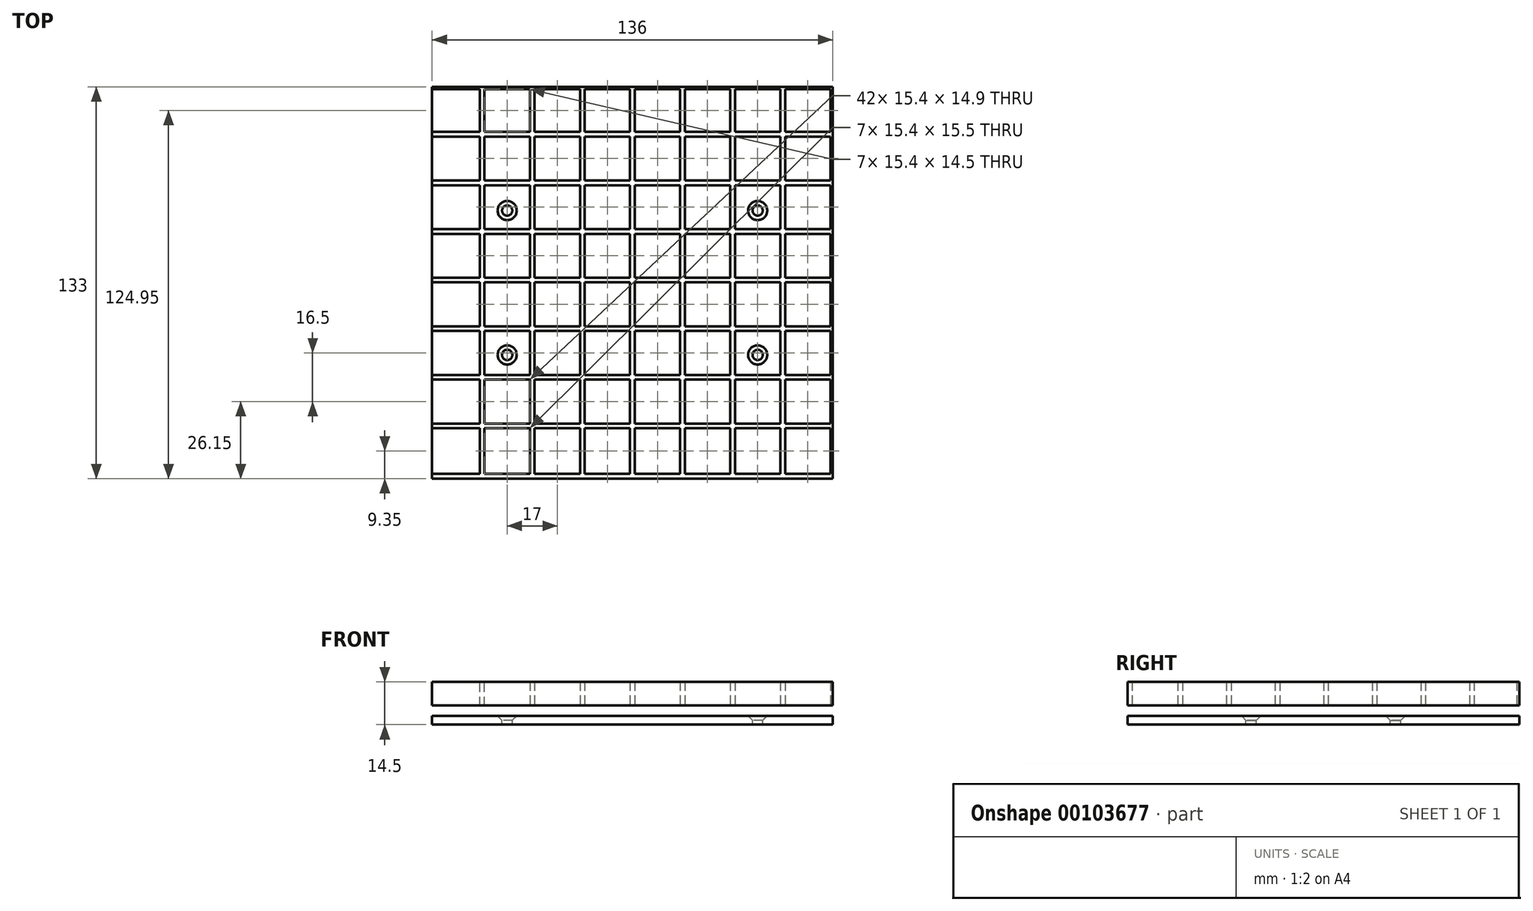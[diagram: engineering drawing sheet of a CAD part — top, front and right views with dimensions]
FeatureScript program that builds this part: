
annotation { "Feature Type Name" : "Feature", "Feature Type Description" : "" }
export const myFeature = defineFeature(function(context is Context, id is Id, definition is map)
    precondition{}
    {
        {
            var Q0;
            Q0=qCreatedBy(makeId("Front.planeOp"),FACE);
            var sketch = newSketch(context, id + "F0", { "sketchPlane" : qUnion([Q0])});
            skLineSegment(sketch, "E0.bottom", {"start": v(-68, 3) * mm, "end": v(68, 3) * mm});
            skLineSegment(sketch, "E0.top", {"start": v(-68, 0) * mm, "end": v(68, 0) * mm});
            skLineSegment(sketch, "E0.left", {"start": v(-68, 3) * mm, "end": v(-68, 0) * mm});
            skLineSegment(sketch, "E0.right", {"start": v(68, 3) * mm, "end": v(68, 0) * mm});
            skLineSegment(sketch, "E1.bottom", {"start": v(-68, 3) * mm, "end": v(-64.5, 3) * mm});
            skLineSegment(sketch, "E1.top", {"start": v(-68, 6.5) * mm, "end": v(-64.5, 6.5) * mm});
            skLineSegment(sketch, "E1.left", {"start": v(-68, 3) * mm, "end": v(-68, 6.5) * mm});
            skLineSegment(sketch, "E1.right", {"start": v(-64.5, 3) * mm, "end": v(-64.5, 6.5) * mm});
            skLineSegment(sketch, "E2.bottom", {"start": v(-20.5, 3) * mm, "end": v(-13.5, 3) * mm});
            skLineSegment(sketch, "E2.top", {"start": v(-20.5, 6.5) * mm, "end": v(-13.5, 6.5) * mm});
            skLineSegment(sketch, "E2.left", {"start": v(-20.5, 3) * mm, "end": v(-20.5, 6.5) * mm});
            skLineSegment(sketch, "E2.right", {"start": v(-13.5, 3) * mm, "end": v(-13.5, 6.5) * mm});
            skLineSegment(sketch, "E3.bottom", {"start": v(68, 3) * mm, "end": v(64.5, 3) * mm});
            skLineSegment(sketch, "E3.top", {"start": v(68, 6.5) * mm, "end": v(64.5, 6.5) * mm});
            skLineSegment(sketch, "E3.left", {"start": v(68, 3) * mm, "end": v(68, 6.5) * mm});
            skLineSegment(sketch, "E3.right", {"start": v(64.5, 3) * mm, "end": v(64.5, 6.5) * mm});
            skLineSegment(sketch, "E4.bottom", {"start": v(-54.5, 3) * mm, "end": v(-47.5, 3) * mm});
            skLineSegment(sketch, "E4.top", {"start": v(-54.5, 6.5) * mm, "end": v(-47.5, 6.5) * mm});
            skLineSegment(sketch, "E4.left", {"start": v(-54.5, 3) * mm, "end": v(-54.5, 6.5) * mm});
            skLineSegment(sketch, "E4.right", {"start": v(-47.5, 3) * mm, "end": v(-47.5, 6.5) * mm});
            skLineSegment(sketch, "E5.bottom", {"start": v(-37.5, 3) * mm, "end": v(-30.5, 3) * mm});
            skLineSegment(sketch, "E5.top", {"start": v(-37.5, 6.5) * mm, "end": v(-30.5, 6.5) * mm});
            skLineSegment(sketch, "E5.left", {"start": v(-37.5, 3) * mm, "end": v(-37.5, 6.5) * mm});
            skLineSegment(sketch, "E5.right", {"start": v(-30.5, 3) * mm, "end": v(-30.5, 6.5) * mm});
            skLineSegment(sketch, "E6.bottom", {"start": v(-3.5, 3) * mm, "end": v(3.5, 3) * mm});
            skLineSegment(sketch, "E6.top", {"start": v(-3.5, 6.5) * mm, "end": v(3.5, 6.5) * mm});
            skLineSegment(sketch, "E6.left", {"start": v(-3.5, 3) * mm, "end": v(-3.5, 6.5) * mm});
            skLineSegment(sketch, "E6.right", {"start": v(3.5, 3) * mm, "end": v(3.5, 6.5) * mm});
            skLineSegment(sketch, "E7.bottom", {"start": v(13.5, 3) * mm, "end": v(20.5, 3) * mm});
            skLineSegment(sketch, "E7.top", {"start": v(13.5, 6.5) * mm, "end": v(20.5, 6.5) * mm});
            skLineSegment(sketch, "E7.left", {"start": v(13.5, 3) * mm, "end": v(13.5, 6.5) * mm});
            skLineSegment(sketch, "E7.right", {"start": v(20.5, 3) * mm, "end": v(20.5, 6.5) * mm});
            skLineSegment(sketch, "E8.bottom", {"start": v(30.5, 3) * mm, "end": v(37.5, 3) * mm});
            skLineSegment(sketch, "E8.top", {"start": v(30.5, 6.5) * mm, "end": v(37.5, 6.5) * mm});
            skLineSegment(sketch, "E8.left", {"start": v(30.5, 3) * mm, "end": v(30.5, 6.5) * mm});
            skLineSegment(sketch, "E8.right", {"start": v(37.5, 3) * mm, "end": v(37.5, 6.5) * mm});
            skLineSegment(sketch, "E9.bottom", {"start": v(47.5, 3) * mm, "end": v(54.5, 3) * mm});
            skLineSegment(sketch, "E9.top", {"start": v(47.5, 6.5) * mm, "end": v(54.5, 6.5) * mm});
            skLineSegment(sketch, "E9.left", {"start": v(47.5, 3) * mm, "end": v(47.5, 6.5) * mm});
            skLineSegment(sketch, "E9.right", {"start": v(54.5, 3) * mm, "end": v(54.5, 6.5) * mm});
            skSolve(sketch);
        }
        {
            var Q0;
            Q0=makeQuery(id+"F0.imprint","IMPRINT",FACE,{"disambiguationData":[TD([[makeQuery(id+"F0.imprint","IMPRINT",EDGE,{"derivedFrom":sQuery(id+"F0.wireOp",EDGE,"E1.bottom")}),1.0]])]});
            var Q1;
            Q1=makeQuery(id+"F0.imprint","IMPRINT",FACE,{"disambiguationData":[TD([[makeQuery(id+"F0.imprint","IMPRINT",EDGE,{"derivedFrom":sQuery(id+"F0.wireOp",EDGE,"E2.bottom")}),1.0]])]});
            var Q2;
            Q2=makeQuery(id+"F0.imprint","IMPRINT",FACE,{"disambiguationData":[TD([[makeQuery(id+"F0.imprint","IMPRINT",EDGE,{"derivedFrom":sQuery(id+"F0.wireOp",EDGE,"E3.bottom")}),-1.0]])]});
            var Q3;
            Q3=makeQuery(id+"F0.imprint","IMPRINT",FACE,{"disambiguationData":[TD([[makeQuery(id+"F0.imprint","IMPRINT",EDGE,{"derivedFrom":sQuery(id+"F0.wireOp",EDGE,"E0.top")}),1.0]])]});
            var Q4;
            Q4=makeQuery(id+"F0.imprint","IMPRINT",FACE,{"disambiguationData":[TD([[makeQuery(id+"F0.imprint","IMPRINT",EDGE,{"derivedFrom":sQuery(id+"F0.wireOp",EDGE,"E4.bottom")}),1.0]])]});
            var Q5;
            Q5=makeQuery(id+"F0.imprint","IMPRINT",FACE,{"disambiguationData":[TD([[makeQuery(id+"F0.imprint","IMPRINT",EDGE,{"derivedFrom":sQuery(id+"F0.wireOp",EDGE,"E5.bottom")}),1.0]])]});
            var Q6;
            Q6=makeQuery(id+"F0.imprint","IMPRINT",FACE,{"disambiguationData":[TD([[makeQuery(id+"F0.imprint","IMPRINT",EDGE,{"derivedFrom":sQuery(id+"F0.wireOp",EDGE,"E6.bottom")}),1.0]])]});
            var Q7;
            Q7=makeQuery(id+"F0.imprint","IMPRINT",FACE,{"disambiguationData":[TD([[makeQuery(id+"F0.imprint","IMPRINT",EDGE,{"derivedFrom":sQuery(id+"F0.wireOp",EDGE,"E7.bottom")}),1.0]])]});
            var Q8;
            Q8=makeQuery(id+"F0.imprint","IMPRINT",FACE,{"disambiguationData":[TD([[makeQuery(id+"F0.imprint","IMPRINT",EDGE,{"derivedFrom":sQuery(id+"F0.wireOp",EDGE,"E8.bottom")}),1.0]])]});
            var Q9;
            Q9=makeQuery(id+"F0.imprint","IMPRINT",FACE,{"disambiguationData":[TD([[makeQuery(id+"F0.imprint","IMPRINT",EDGE,{"derivedFrom":sQuery(id+"F0.wireOp",EDGE,"E9.bottom")}),1.0]])]});
            extrude(context, id + "F1", {"entities" : qUnion([Q0, Q1, Q2, Q3, Q4, Q5, Q6, Q7, Q8, Q9]), "depth" : 133 * mm});
        }
        {
            var Q0;
            Q0=makeQuery(id+"F1.opExtrude","CAP_FACE",FACE,{"disambiguationData":[OSD([sQuery(id+"F0.wireOp",EDGE,"E0.bottom"),sQuery(id+"F0.wireOp",EDGE,"E0.top"),sQuery(id+"F0.wireOp",EDGE,"E0.left"),sQuery(id+"F0.wireOp",EDGE,"E0.right"),sQuery(id+"F0.wireOp",EDGE,"E1.top"),sQuery(id+"F0.wireOp",EDGE,"E1.left"),sQuery(id+"F0.wireOp",EDGE,"E1.right"),sQuery(id+"F0.wireOp",EDGE,"E2.top"),sQuery(id+"F0.wireOp",EDGE,"E2.left"),sQuery(id+"F0.wireOp",EDGE,"E2.right"),sQuery(id+"F0.wireOp",EDGE,"E3.top"),sQuery(id+"F0.wireOp",EDGE,"E3.left"),sQuery(id+"F0.wireOp",EDGE,"E3.right"),sQuery(id+"F0.wireOp",EDGE,"E4.top"),sQuery(id+"F0.wireOp",EDGE,"E4.left"),sQuery(id+"F0.wireOp",EDGE,"E4.right"),sQuery(id+"F0.wireOp",EDGE,"E5.top"),sQuery(id+"F0.wireOp",EDGE,"E5.left"),sQuery(id+"F0.wireOp",EDGE,"E5.right"),sQuery(id+"F0.wireOp",EDGE,"E6.top"),sQuery(id+"F0.wireOp",EDGE,"E6.left"),sQuery(id+"F0.wireOp",EDGE,"E6.right"),sQuery(id+"F0.wireOp",EDGE,"E7.top"),sQuery(id+"F0.wireOp",EDGE,"E7.left"),sQuery(id+"F0.wireOp",EDGE,"E7.right"),sQuery(id+"F0.wireOp",EDGE,"E8.top"),sQuery(id+"F0.wireOp",EDGE,"E8.left"),sQuery(id+"F0.wireOp",EDGE,"E8.right"),sQuery(id+"F0.wireOp",EDGE,"E9.top"),sQuery(id+"F0.wireOp",EDGE,"E9.left"),sQuery(id+"F0.wireOp",EDGE,"E9.right")])],"isStart":false});
            var sketch = newSketch(context, id + "F2", { "sketchPlane" : qUnion([Q0])});
            skLineSegment(sketch, "E10.bottom", {"start": v(-66.4, 6.5) * mm, "end": v(-68, 6.5) * mm});
            skLineSegment(sketch, "E10.top", {"start": v(-66.4, 14.5) * mm, "end": v(-68, 14.5) * mm});
            skLineSegment(sketch, "E10.left", {"start": v(-66.4, 6.5) * mm, "end": v(-66.4, 14.5) * mm});
            skLineSegment(sketch, "E10.right", {"start": v(-68, 6.5) * mm, "end": v(-68, 14.5) * mm});
            skLineSegment(sketch, "E11.bottom", {"start": v(-51.8, 6.5) * mm, "end": v(-50.2, 6.5) * mm});
            skLineSegment(sketch, "E11.top", {"start": v(-51.8, 14.5) * mm, "end": v(-50.2, 14.5) * mm});
            skLineSegment(sketch, "E11.left", {"start": v(-51.8, 6.5) * mm, "end": v(-51.8, 14.5) * mm});
            skLineSegment(sketch, "E11.right", {"start": v(-50.2, 6.5) * mm, "end": v(-50.2, 14.5) * mm});
            skLineSegment(sketch, "E12.1.0.0", {"start": v(-34.8, 6.5) * mm, "end": v(-34.8, 14.5) * mm});
            skLineSegment(sketch, "E12.1.0.1", {"start": v(-34.8, 14.5) * mm, "end": v(-33.2, 14.5) * mm});
            skLineSegment(sketch, "E12.1.0.2", {"start": v(-34.8, 6.5) * mm, "end": v(-33.2, 6.5) * mm});
            skLineSegment(sketch, "E12.1.0.3", {"start": v(-33.2, 6.5) * mm, "end": v(-33.2, 14.5) * mm});
            skLineSegment(sketch, "E12.2.0.0", {"start": v(-17.8, 6.5) * mm, "end": v(-17.8, 14.5) * mm});
            skLineSegment(sketch, "E12.2.0.1", {"start": v(-17.8, 14.5) * mm, "end": v(-16.2, 14.5) * mm});
            skLineSegment(sketch, "E12.2.0.2", {"start": v(-17.8, 6.5) * mm, "end": v(-16.2, 6.5) * mm});
            skLineSegment(sketch, "E12.2.0.3", {"start": v(-16.2, 6.5) * mm, "end": v(-16.2, 14.5) * mm});
            skLineSegment(sketch, "E12.3.0.0", {"start": v(-0.8, 6.5) * mm, "end": v(-0.8, 14.5) * mm});
            skLineSegment(sketch, "E12.3.0.1", {"start": v(-0.8, 14.5) * mm, "end": v(0.8, 14.5) * mm});
            skLineSegment(sketch, "E12.3.0.2", {"start": v(-0.8, 6.5) * mm, "end": v(0.8, 6.5) * mm});
            skLineSegment(sketch, "E12.3.0.3", {"start": v(0.8, 6.5) * mm, "end": v(0.8, 14.5) * mm});
            skLineSegment(sketch, "E12.4.0.0", {"start": v(16.2, 6.5) * mm, "end": v(16.2, 14.5) * mm});
            skLineSegment(sketch, "E12.4.0.1", {"start": v(16.2, 14.5) * mm, "end": v(17.8, 14.5) * mm});
            skLineSegment(sketch, "E12.4.0.2", {"start": v(16.2, 6.5) * mm, "end": v(17.8, 6.5) * mm});
            skLineSegment(sketch, "E12.4.0.3", {"start": v(17.8, 6.5) * mm, "end": v(17.8, 14.5) * mm});
            skLineSegment(sketch, "E12.5.0.0", {"start": v(33.2, 6.5) * mm, "end": v(33.2, 14.5) * mm});
            skLineSegment(sketch, "E12.5.0.1", {"start": v(33.2, 14.5) * mm, "end": v(34.8, 14.5) * mm});
            skLineSegment(sketch, "E12.5.0.2", {"start": v(33.2, 6.5) * mm, "end": v(34.8, 6.5) * mm});
            skLineSegment(sketch, "E12.5.0.3", {"start": v(34.8, 6.5) * mm, "end": v(34.8, 14.5) * mm});
            skLineSegment(sketch, "E12.direction1", {"start": v(-51.8, 6.5) * mm, "end": v(-34.8, 6.5) * mm, "construction": true});
            skPoint(sketch, "E13", {"position": v(-34, 6.5) * mm});
            skLineSegment(sketch, "E14.0.6.0", {"start": v(50.2, 6.5) * mm, "end": v(50.2, 14.5) * mm});
            skLineSegment(sketch, "E14.3.6.0", {"start": v(50.2, 14.5) * mm, "end": v(51.8, 14.5) * mm});
            skLineSegment(sketch, "E14.6.6.0", {"start": v(50.2, 6.5) * mm, "end": v(51.8, 6.5) * mm});
            skLineSegment(sketch, "E14.9.6.0", {"start": v(51.8, 6.5) * mm, "end": v(51.8, 14.5) * mm});
            skLineSegment(sketch, "E15.bottom", {"start": v(68, 6.5) * mm, "end": v(67.2, 6.5) * mm});
            skLineSegment(sketch, "E15.top", {"start": v(68, 14.5) * mm, "end": v(67.2, 14.5) * mm});
            skLineSegment(sketch, "E15.left", {"start": v(68, 6.5) * mm, "end": v(68, 14.5) * mm});
            skLineSegment(sketch, "E15.right", {"start": v(67.2, 6.5) * mm, "end": v(67.2, 14.5) * mm});
            skSolve(sketch);
        }
        {
            var Q0;
            Q0=makeQuery(id+"F2.imprint","IMPRINT",FACE,{"disambiguationData":[TD([[makeQuery(id+"F2.imprint","IMPRINT",EDGE,{"derivedFrom":sQuery(id+"F2.wireOp",EDGE,"E10.bottom")}),1.0]])]});
            var Q1;
            Q1=makeQuery(id+"F2.imprint","IMPRINT",FACE,{"disambiguationData":[TD([[makeQuery(id+"F2.imprint","IMPRINT",EDGE,{"derivedFrom":sQuery(id+"F2.wireOp",EDGE,"E11.bottom")}),1.0]])]});
            var Q2;
            Q2=makeQuery(id+"F2.imprint","IMPRINT",FACE,{"disambiguationData":[TD([[makeQuery(id+"F2.imprint","IMPRINT",EDGE,{"derivedFrom":sQuery(id+"F2.wireOp",EDGE,"E12.1.0.0")}),-1.0]])]});
            var Q3;
            Q3=makeQuery(id+"F2.imprint","IMPRINT",FACE,{"disambiguationData":[TD([[makeQuery(id+"F2.imprint","IMPRINT",EDGE,{"derivedFrom":sQuery(id+"F2.wireOp",EDGE,"E12.2.0.0")}),-1.0]])]});
            var Q4;
            Q4=makeQuery(id+"F2.imprint","IMPRINT",FACE,{"disambiguationData":[TD([[makeQuery(id+"F2.imprint","IMPRINT",EDGE,{"derivedFrom":sQuery(id+"F2.wireOp",EDGE,"E12.3.0.0")}),-1.0]])]});
            var Q5;
            Q5=makeQuery(id+"F2.imprint","IMPRINT",FACE,{"disambiguationData":[TD([[makeQuery(id+"F2.imprint","IMPRINT",EDGE,{"derivedFrom":sQuery(id+"F2.wireOp",EDGE,"E12.4.0.0")}),-1.0]])]});
            var Q6;
            Q6=makeQuery(id+"F2.imprint","IMPRINT",FACE,{"disambiguationData":[TD([[makeQuery(id+"F2.imprint","IMPRINT",EDGE,{"derivedFrom":sQuery(id+"F2.wireOp",EDGE,"E12.5.0.0")}),-1.0]])]});
            var Q7;
            Q7=makeQuery(id+"F2.imprint","IMPRINT",FACE,{"disambiguationData":[TD([[makeQuery(id+"F2.imprint","IMPRINT",EDGE,{"derivedFrom":sQuery(id+"F2.wireOp",EDGE,"E14.0.6.0")}),-1.0]])]});
            var Q8;
            Q8=makeQuery(id+"F2.imprint","IMPRINT",FACE,{"disambiguationData":[TD([[makeQuery(id+"F2.imprint","IMPRINT",EDGE,{"derivedFrom":sQuery(id+"F2.wireOp",EDGE,"E15.bottom")}),-1.0]])]});
            var Q9;
            Q9=makeQuery(id+"F1.opExtrude","CAP_FACE",FACE,{"disambiguationData":[OSD([sQuery(id+"F0.wireOp",EDGE,"E0.bottom"),sQuery(id+"F0.wireOp",EDGE,"E0.top"),sQuery(id+"F0.wireOp",EDGE,"E0.left"),sQuery(id+"F0.wireOp",EDGE,"E0.right"),sQuery(id+"F0.wireOp",EDGE,"E1.top"),sQuery(id+"F0.wireOp",EDGE,"E1.left"),sQuery(id+"F0.wireOp",EDGE,"E1.right"),sQuery(id+"F0.wireOp",EDGE,"E2.top"),sQuery(id+"F0.wireOp",EDGE,"E2.left"),sQuery(id+"F0.wireOp",EDGE,"E2.right"),sQuery(id+"F0.wireOp",EDGE,"E3.top"),sQuery(id+"F0.wireOp",EDGE,"E3.left"),sQuery(id+"F0.wireOp",EDGE,"E3.right"),sQuery(id+"F0.wireOp",EDGE,"E4.top"),sQuery(id+"F0.wireOp",EDGE,"E4.left"),sQuery(id+"F0.wireOp",EDGE,"E4.right"),sQuery(id+"F0.wireOp",EDGE,"E5.top"),sQuery(id+"F0.wireOp",EDGE,"E5.left"),sQuery(id+"F0.wireOp",EDGE,"E5.right"),sQuery(id+"F0.wireOp",EDGE,"E6.top"),sQuery(id+"F0.wireOp",EDGE,"E6.left"),sQuery(id+"F0.wireOp",EDGE,"E6.right"),sQuery(id+"F0.wireOp",EDGE,"E7.top"),sQuery(id+"F0.wireOp",EDGE,"E7.left"),sQuery(id+"F0.wireOp",EDGE,"E7.right"),sQuery(id+"F0.wireOp",EDGE,"E8.top"),sQuery(id+"F0.wireOp",EDGE,"E8.left"),sQuery(id+"F0.wireOp",EDGE,"E8.right"),sQuery(id+"F0.wireOp",EDGE,"E9.top"),sQuery(id+"F0.wireOp",EDGE,"E9.left"),sQuery(id+"F0.wireOp",EDGE,"E9.right")])],"isStart":true});
            extrude(context, id + "F3", {"entities" : qUnion([Q0, Q1, Q2, Q3, Q4, Q5, Q6, Q7, Q8]), "operationType" : NewBodyOperationType.ADD, "endBound" : BoundingType.UP_TO_SURFACE, "oppositeDirection" : true, "endBoundEntityFace" : qUnion([Q9]), "depth" : 25 * mm});
        }
        {
            var Q0;
            Q0=makeQuery(id+"F3.boolean.opBoolean","MERGE",FACE,{"derivedFrom":[makeQuery(id+"F1.opExtrude","SWEPT_FACE",FACE,{"disambiguationData":[OSD([sQuery(id+"F0.wireOp",EDGE,"E0.left"),sQuery(id+"F0.wireOp",EDGE,"E1.left")])]}),makeQuery(id+"F3.opExtrude","SWEPT_FACE",FACE,{"disambiguationData":[OSD([sQuery(id+"F2.wireOp",EDGE,"E10.right")])]})]});
            var sketch = newSketch(context, id + "F4", { "sketchPlane" : qUnion([Q0])});
            skLineSegment(sketch, "E16.bottom", {"start": v(0, 14.5) * mm, "end": v(0.8, 14.5) * mm});
            skLineSegment(sketch, "E16.top", {"start": v(0, 6.5) * mm, "end": v(0.8, 6.5) * mm});
            skLineSegment(sketch, "E16.left", {"start": v(0, 14.5) * mm, "end": v(0, 6.5) * mm});
            skLineSegment(sketch, "E16.right", {"start": v(0.8, 14.5) * mm, "end": v(0.8, 6.5) * mm});
            skLineSegment(sketch, "E17.bottom", {"start": v(15.3, 14.5) * mm, "end": v(16.9, 14.5) * mm});
            skLineSegment(sketch, "E17.top", {"start": v(15.3, 6.5) * mm, "end": v(16.9, 6.5) * mm});
            skLineSegment(sketch, "E17.left", {"start": v(15.3, 14.5) * mm, "end": v(15.3, 6.5) * mm});
            skLineSegment(sketch, "E17.right", {"start": v(16.9, 14.5) * mm, "end": v(16.9, 6.5) * mm});
            skLineSegment(sketch, "E18.1.0.0", {"start": v(33.4, 14.5) * mm, "end": v(33.4, 6.5) * mm});
            skLineSegment(sketch, "E18.1.0.1", {"start": v(31.8, 14.5) * mm, "end": v(31.8, 6.5) * mm});
            skLineSegment(sketch, "E18.1.0.2", {"start": v(31.8, 14.5) * mm, "end": v(33.4, 14.5) * mm});
            skLineSegment(sketch, "E18.1.0.3", {"start": v(31.8, 6.5) * mm, "end": v(33.4, 6.5) * mm});
            skLineSegment(sketch, "E18.2.0.0", {"start": v(49.9, 14.5) * mm, "end": v(49.9, 6.5) * mm});
            skLineSegment(sketch, "E18.2.0.1", {"start": v(48.3, 14.5) * mm, "end": v(48.3, 6.5) * mm});
            skLineSegment(sketch, "E18.2.0.2", {"start": v(48.3, 14.5) * mm, "end": v(49.9, 14.5) * mm});
            skLineSegment(sketch, "E18.2.0.3", {"start": v(48.3, 6.5) * mm, "end": v(49.9, 6.5) * mm});
            skLineSegment(sketch, "E18.3.0.0", {"start": v(66.4, 14.5) * mm, "end": v(66.4, 6.5) * mm});
            skLineSegment(sketch, "E18.3.0.1", {"start": v(64.8, 14.5) * mm, "end": v(64.8, 6.5) * mm});
            skLineSegment(sketch, "E18.3.0.2", {"start": v(64.8, 14.5) * mm, "end": v(66.4, 14.5) * mm});
            skLineSegment(sketch, "E18.3.0.3", {"start": v(64.8, 6.5) * mm, "end": v(66.4, 6.5) * mm});
            skLineSegment(sketch, "E18.4.0.0", {"start": v(82.9, 14.5) * mm, "end": v(82.9, 6.5) * mm});
            skLineSegment(sketch, "E18.4.0.1", {"start": v(81.3, 14.5) * mm, "end": v(81.3, 6.5) * mm});
            skLineSegment(sketch, "E18.4.0.2", {"start": v(81.3, 14.5) * mm, "end": v(82.9, 14.5) * mm});
            skLineSegment(sketch, "E18.4.0.3", {"start": v(81.3, 6.5) * mm, "end": v(82.9, 6.5) * mm});
            skLineSegment(sketch, "E18.5.0.0", {"start": v(99.4, 14.5) * mm, "end": v(99.4, 6.5) * mm});
            skLineSegment(sketch, "E18.5.0.1", {"start": v(97.8, 14.5) * mm, "end": v(97.8, 6.5) * mm});
            skLineSegment(sketch, "E18.5.0.2", {"start": v(97.8, 14.5) * mm, "end": v(99.4, 14.5) * mm});
            skLineSegment(sketch, "E18.5.0.3", {"start": v(97.8, 6.5) * mm, "end": v(99.4, 6.5) * mm});
            skLineSegment(sketch, "E18.6.0.0", {"start": v(115.9, 14.5) * mm, "end": v(115.9, 6.5) * mm});
            skLineSegment(sketch, "E18.6.0.1", {"start": v(114.3, 14.5) * mm, "end": v(114.3, 6.5) * mm});
            skLineSegment(sketch, "E18.6.0.2", {"start": v(114.3, 14.5) * mm, "end": v(115.9, 14.5) * mm});
            skLineSegment(sketch, "E18.6.0.3", {"start": v(114.3, 6.5) * mm, "end": v(115.9, 6.5) * mm});
            skLineSegment(sketch, "E18.direction1", {"start": v(16.9, 6.5) * mm, "end": v(33.4, 6.5) * mm, "construction": true});
            skLineSegment(sketch, "E19.bottom", {"start": v(131.4, 14.5) * mm, "end": v(133, 14.5) * mm});
            skLineSegment(sketch, "E19.top", {"start": v(131.4, 6.5) * mm, "end": v(133, 6.5) * mm});
            skLineSegment(sketch, "E19.left", {"start": v(131.4, 14.5) * mm, "end": v(131.4, 6.5) * mm});
            skLineSegment(sketch, "E19.right", {"start": v(133, 14.5) * mm, "end": v(133, 6.5) * mm});
            skSolve(sketch);
        }
        {
            var Q0;
            Q0=qSketchRegion(id+"F4",true);
            var Q1;
            Q1=makeQuery(id+"F3.boolean.opBoolean","MERGE",FACE,{"derivedFrom":[makeQuery(id+"F1.opExtrude","SWEPT_FACE",FACE,{"disambiguationData":[OSD([sQuery(id+"F0.wireOp",EDGE,"E0.right"),sQuery(id+"F0.wireOp",EDGE,"E3.left")])]}),makeQuery(id+"F3.opExtrude","SWEPT_FACE",FACE,{"disambiguationData":[OSD([sQuery(id+"F2.wireOp",EDGE,"E15.left")])]})]});
            extrude(context, id + "F5", {"entities" : qUnion([Q0]), "operationType" : NewBodyOperationType.ADD, "endBound" : BoundingType.UP_TO_SURFACE, "oppositeDirection" : true, "endBoundEntityFace" : qUnion([Q1]), "depth" : 25 * mm});
        }
        {
            var Q0;
            {var subQ0=sQuery(id+"F0.wireOp",EDGE,"E0.bottom");Q0=makeQuery(id+"F1.opExtrude","SWEPT_FACE",FACE,{"disambiguationData":[OSD([subQ0]),TDD([makeQuery(id+"F0.imprint","IMPRINT",EDGE,{"disambiguationData":[TD([[makeQuery(id+"F0.imprint","INTERSECT",VERTEX,{"derivedFrom":[subQ0,sQuery(id+"F0.wireOp",EDGE,"E4.bottom"),sQuery(id+"F0.wireOp",EDGE,"E4.right")]}),-1.0]])],"derivedFrom":subQ0})])]});}
            var sketch = newSketch(context, id + "F6", { "sketchPlane" : qUnion([Q0])});
            skPoint(sketch, "E20.startSnap0", {"position": v(-42.5, 0) * mm});
            skLineSegment(sketch, "E21", {"start": v(-42.5, -133) * mm, "end": v(-42.5, 0) * mm, "construction": true});
            skPoint(sketch, "E22", {"position": v(-42.5, -91) * mm});
            skPoint(sketch, "E23", {"position": v(-42.5, -42) * mm});
            skLineSegment(sketch, "E24", {"start": v(0, 0) * mm, "end": v(0, -133.94) * mm, "construction": true});
            skPoint(sketch, "E25.MirrorP", {"position": v(42.5, -42) * mm});
            skPoint(sketch, "E26.MirrorP", {"position": v(42.5, -91) * mm});
            skSolve(sketch);
        }
        {
            var Q0;
            {var subQ0=sQuery(id+"F0.wireOp",EDGE,"E0.bottom");Q0=makeQuery(id+"F1.opExtrude","SWEPT_FACE",FACE,{"disambiguationData":[OSD([subQ0]),TDD([makeQuery(id+"F0.imprint","IMPRINT",EDGE,{"disambiguationData":[TD([[makeQuery(id+"F0.imprint","INTERSECT",VERTEX,{"derivedFrom":[subQ0,sQuery(id+"F0.wireOp",EDGE,"E8.bottom"),sQuery(id+"F0.wireOp",EDGE,"E8.right")]}),-1.0]])],"derivedFrom":subQ0})])]});}
            var sketch = newSketch(context, id + "F7", { "sketchPlane" : qUnion([Q0])});
            skLineSegment(sketch, "E27", {"start": v(42.5, 0) * mm, "end": v(42.5, -133) * mm, "construction": true});
            skPoint(sketch, "E28", {"position": v(42.5, -66.5) * mm});
            skLineSegment(sketch, "E29", {"start": v(37.5, -66.5) * mm, "end": v(47.5, -66.5) * mm, "construction": true});
            skPoint(sketch, "E30", {"position": v(42.5, -42) * mm});
            skLineSegment(sketch, "E31.MirrorCS", {"start": v(47.5, -66.5) * mm, "end": v(37.5, -66.5) * mm, "construction": true});
            skPoint(sketch, "E32.MirrorP", {"position": v(42.5, -91) * mm});
            skSolve(sketch);
        }
        {
            var Q0;
            Q0=sQuery(id+"F6.wireOp",VERTEX,"f3366a95-9c4d-4f63-b918-8e86c8d0df700.MirrorP");
            var Q1;
            Q1=sQuery(id+"F6.wireOp",VERTEX,"a1fa1e25-132a-45b0-a503-2720dc40e21a");
            var Q2;
            Q2=sQuery(id+"F7.wireOp",VERTEX,"E30");
            var Q3;
            Q3=sQuery(id+"F7.wireOp",VERTEX,"E32.MirrorP");
            var Q4;
            Q4=sQuery(id+"F6.wireOp",VERTEX,"E23");
            var Q5;
            Q5=sQuery(id+"F6.wireOp",VERTEX,"E22");
            var Q6;
            Q6=makeQuery(id+"F1.opExtrude","SWEPT_BODY",BODY,{"disambiguationData":[OSD([sQuery(id+"F0.wireOp",EDGE,"E0.bottom"),sQuery(id+"F0.wireOp",EDGE,"E0.top"),sQuery(id+"F0.wireOp",EDGE,"E0.left"),sQuery(id+"F0.wireOp",EDGE,"E0.right"),sQuery(id+"F0.wireOp",EDGE,"E1.top"),sQuery(id+"F0.wireOp",EDGE,"E1.left"),sQuery(id+"F0.wireOp",EDGE,"E1.right"),sQuery(id+"F0.wireOp",EDGE,"E2.top"),sQuery(id+"F0.wireOp",EDGE,"E2.left"),sQuery(id+"F0.wireOp",EDGE,"E2.right"),sQuery(id+"F0.wireOp",EDGE,"E3.top"),sQuery(id+"F0.wireOp",EDGE,"E3.left"),sQuery(id+"F0.wireOp",EDGE,"E3.right"),sQuery(id+"F0.wireOp",EDGE,"E4.top"),sQuery(id+"F0.wireOp",EDGE,"E4.left"),sQuery(id+"F0.wireOp",EDGE,"E4.right"),sQuery(id+"F0.wireOp",EDGE,"E5.top"),sQuery(id+"F0.wireOp",EDGE,"E5.left"),sQuery(id+"F0.wireOp",EDGE,"E5.right"),sQuery(id+"F0.wireOp",EDGE,"E6.top"),sQuery(id+"F0.wireOp",EDGE,"E6.left"),sQuery(id+"F0.wireOp",EDGE,"E6.right"),sQuery(id+"F0.wireOp",EDGE,"E7.top"),sQuery(id+"F0.wireOp",EDGE,"E7.left"),sQuery(id+"F0.wireOp",EDGE,"E7.right"),sQuery(id+"F0.wireOp",EDGE,"E8.top"),sQuery(id+"F0.wireOp",EDGE,"E8.left"),sQuery(id+"F0.wireOp",EDGE,"E8.right"),sQuery(id+"F0.wireOp",EDGE,"E9.top"),sQuery(id+"F0.wireOp",EDGE,"E9.left"),sQuery(id+"F0.wireOp",EDGE,"E9.right")])]});
            hole(context, id + "F8", {"style" : HoleStyle.C_SINK, "endStyle" : HoleEndStyle.BLIND, "holeDiameter" : 3.5 * mm, "cSinkDiameter" : 6.5 * mm, "cSinkAngle" : 90 * degree, "holeDepth" : 12 * mm, "tappedDepth" : 12 * mm, "tapClearance" : 3, "locations" : qUnion([Q0, Q1, Q2, Q3, Q4, Q5]), "scope" : qUnion([Q6])});
        }
    });
